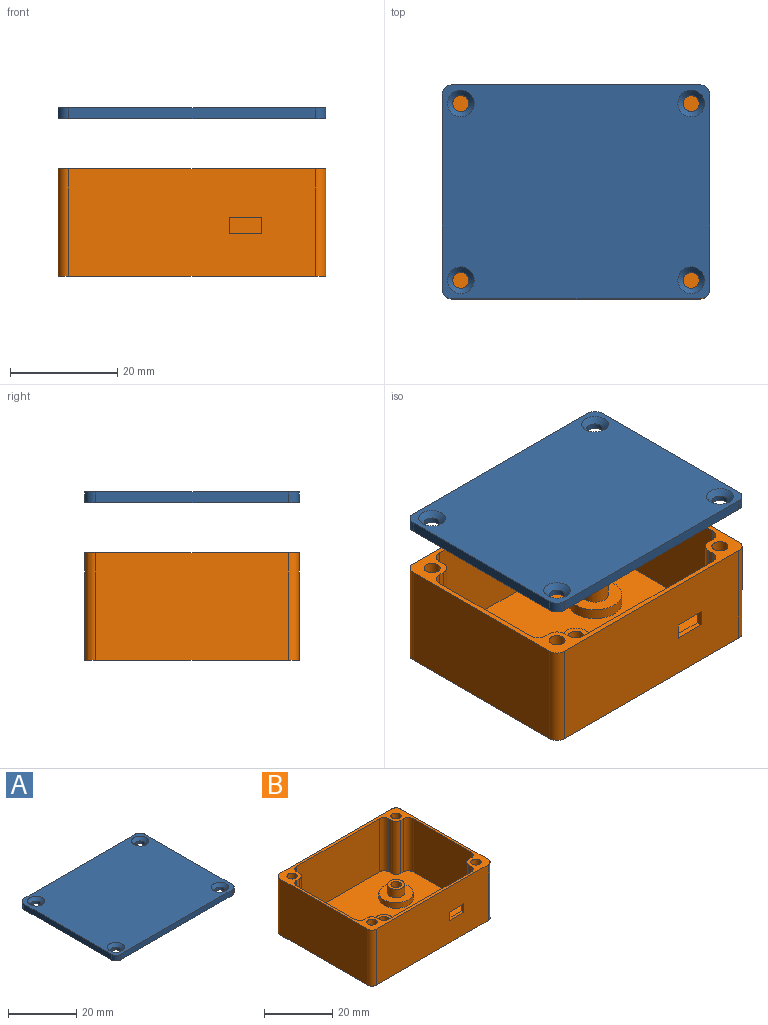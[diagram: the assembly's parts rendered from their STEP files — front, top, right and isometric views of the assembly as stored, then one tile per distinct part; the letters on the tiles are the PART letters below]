
ASSEMBLY  parts=2 mates=1
PART A: 18 faces, bbox 50x40x2 mm
  f0: plane 46x2mm, normal (0,1,0), area 92mm2, adj f4,f5,f14,f17
  f1: plane 36x2mm, normal (-1,0,0), area 72mm2, adj f4,f5,f14,f15
  f2: plane 46x2mm, normal (0,-1,0), area 92mm2, adj f4,f5,f15,f16
  f3: plane 36x2mm, normal (1,0,0), area 72mm2, adj f4,f5,f16,f17
  f4: plane 50x40mm, normal (0,0,1), area 1918mm2, adj f0,f1,f2,f3,f10,f11,f12,f13
  f5: plane 50x40mm, normal (0,0,-1), area 1968.3mm2, adj f0,f1,f2,f3,f6,f7,f8,f9
  f6: cylinder r=1.5mm len=3mm, axis (0,0,1), area 9.4mm2, adj f5,f10
  f7: cylinder r=1.5mm len=3mm, axis (0,0,1), area 9.4mm2, adj f5,f13
  f8: cylinder r=1.5mm len=3mm, axis (0,0,1), area 9.4mm2, adj f5,f12
  f9: cylinder r=1.5mm len=3mm, axis (0,0,1), area 9.4mm2, adj f5,f11
  f10: cone r=1.5mm half-angle=45deg, axis (0,0,1), area 17.8mm2, adj f4,f6
  f11: cone r=1.5mm half-angle=45deg, axis (0,0,1), area 17.8mm2, adj f4,f9
  f12: cone r=1.5mm half-angle=45deg, axis (0,0,1), area 17.8mm2, adj f4,f8
  f13: cone r=1.5mm half-angle=45deg, axis (0,0,1), area 17.8mm2, adj f4,f7
  f14: cylinder r=2mm len=2mm, axis (0,0,1), area 6.3mm2, adj f0,f1,f4,f5
  f15: cylinder r=2mm len=2mm, axis (0,0,-1), area 6.3mm2, adj f1,f2,f4,f5
  f16: cylinder r=2mm len=2mm, axis (0,0,1), area 6.3mm2, adj f2,f3,f4,f5
  f17: cylinder r=2mm len=2mm, axis (0,0,-1), area 6.3mm2, adj f0,f3,f4,f5
PART B: 71 faces, bbox 50x40x20 mm
  f0: plane 34x19mm, normal (0,1,0), area 628mm2, adj f5,f9,f56,f58,f67,f68,f69,f70
  f1: plane 46x20mm, normal (0,-1,0), area 902mm2, adj f2,f9,f52,f53,f67,f68,f69,f70
  f2: plane 50x40mm, normal (0,0,-1), area 1949.8mm2, adj f1,f10,f11,f12,f37,f38,f39,f40
  f3: cylinder r=1.5mm len=4mm, axis (0,0,-1), area 37.7mm2, adj f30,f50
  f4: cylinder r=1.5mm len=4mm, axis (0,0,-1), area 37.7mm2, adj f32,f43
  f5: plane 48x38mm, normal (0,0,1), area 1563.5mm2, adj f0,f6,f7,f8,f13,f14,f15,f16
  f6: plane 24x19mm, normal (1,0,0), area 456mm2, adj f5,f9,f57,f66
  f7: plane 34x19mm, normal (0,-1,0), area 646mm2, adj f5,f9,f62,f64
  f8: plane 24x19mm, normal (-1,0,0), area 456mm2, adj f5,f9,f60,f61
  f9: plane 50x40mm, normal (0,0,1), area 247.7mm2, adj f0,f1,f6,f7,f8,f10,f11,f12
  f10: plane 46x20mm, normal (0,1,0), area 920mm2, adj f2,f9,f51,f54
  f11: plane 36x20mm, normal (-1,0,0), area 720mm2, adj f2,f9,f51,f52
  f12: plane 36x20mm, normal (1,0,0), area 720mm2, adj f2,f9,f53,f54
  f13: plane 19x1mm, normal (0,-1,0), area 19mm2, adj f5,f9,f65,f66
  f14: plane 19x1mm, normal (1,0,0), area 19mm2, adj f5,f9,f64,f65
  f15: plane 19x1mm, normal (0,1,0), area 19mm2, adj f5,f9,f59,f60
  f16: plane 19x1mm, normal (-1,0,0), area 19mm2, adj f5,f9,f58,f59
  f17: plane 19x1mm, normal (0,-1,0), area 19mm2, adj f5,f9,f61,f63
  f18: plane 19x1mm, normal (-1,0,0), area 19mm2, adj f5,f9,f62,f63
  f19: plane 19x1mm, normal (0,1,0), area 19mm2, adj f5,f9,f55,f57
  f20: plane 19x1mm, normal (1,0,0), area 19mm2, adj f5,f9,f55,f56
  f21: cylinder r=1.5mm len=10mm, axis (0,0,1), area 94.2mm2, adj f9,f22
  f22: plane 3x3mm, normal (0,0,1), area 7.1mm2, adj f21
  f23: cylinder r=1.5mm len=10mm, axis (0,0,1), area 94.2mm2, adj f9,f24
  f24: plane 3x3mm, normal (0,0,1), area 7.1mm2, adj f23
  f25: cylinder r=1.5mm len=10mm, axis (0,0,1), area 94.2mm2, adj f9,f26
  f26: plane 3x3mm, normal (0,0,1), area 7.1mm2, adj f25
  f27: cylinder r=1.5mm len=10mm, axis (0,0,1), area 94.2mm2, adj f9,f28
  f28: plane 3x3mm, normal (0,0,1), area 7.1mm2, adj f27
  f29: cylinder r=2.5mm len=5mm, axis (0,0,-1), area 47.1mm2, adj f30,f34
  f30: plane 5x5mm, normal (0,0,1), area 12.6mm2, adj f3,f29
  f31: cylinder r=2.5mm len=5mm, axis (0,0,-1), area 47.1mm2, adj f32,f36
  f32: plane 5x5mm, normal (0,0,1), area 12.6mm2, adj f4,f31
  f33: cylinder r=5mm len=10mm, axis (0,0,-1), area 62.8mm2, adj f5,f34
  f34: plane 10x10mm, normal (0,0,1), area 58.9mm2, adj f29,f33
  f35: cylinder r=5mm len=10mm, axis (0,0,-1), area 62.8mm2, adj f5,f36
  f36: plane 10x10mm, normal (0,0,1), area 58.9mm2, adj f31,f35
  f37: plane 2.84x2mm, normal (-0.95,-0.32,0), area 6mm2, adj f2,f38,f42,f43
  f38: plane 2.26x2mm, normal (-0.75,0.66,0), area 6mm2, adj f2,f37,f39,f43
  f39: plane 2.94x2mm, normal (0.19,0.98,0), area 6mm2, adj f2,f38,f40,f43
  f40: plane 2.84x2mm, normal (0.95,0.32,0), area 6mm2, adj f2,f39,f41,f43
  f41: plane 2.26x2mm, normal (0.75,-0.66,0), area 6mm2, adj f2,f40,f42,f43
  f42: plane 2.94x2mm, normal (-0.19,-0.98,0), area 6mm2, adj f2,f37,f41,f43
  f43: plane 5.89x5.68mm, normal (0,0,-1), area 16.3mm2, adj f4,f37,f38,f39,f40,f41,f42
  f44: plane 3x2mm, normal (-1,-0.04,0), area 6mm2, adj f2,f45,f49,f50
  f45: plane 2.54x2mm, normal (-0.53,0.85,0), area 6mm2, adj f2,f44,f46,f50
  f46: plane 2.65x2mm, normal (0.47,0.88,0), area 6mm2, adj f2,f45,f47,f50
  f47: plane 3x2mm, normal (1,0.04,0), area 6mm2, adj f2,f46,f48,f50
  f48: plane 2.54x2mm, normal (0.53,-0.85,0), area 6mm2, adj f2,f47,f49,f50
  f49: plane 2.65x2mm, normal (-0.47,-0.88,0), area 6mm2, adj f2,f44,f48,f50
  f50: plane 6x5.31mm, normal (0,0,-1), area 16.3mm2, adj f3,f44,f45,f46,f47,f48,f49
  f51: cylinder r=2mm len=20mm, axis (0,0,1), area 62.8mm2, adj f2,f9,f10,f11
  f52: cylinder r=2mm len=20mm, axis (0,0,-1), area 62.8mm2, adj f1,f2,f9,f11
  f53: cylinder r=2mm len=20mm, axis (0,0,1), area 62.8mm2, adj f1,f2,f9,f12
  f54: cylinder r=2mm len=20mm, axis (0,0,-1), area 62.8mm2, adj f2,f9,f10,f12
  f55: cylinder r=2mm len=19mm, axis (0,0,1), area 59.7mm2, adj f5,f9,f19,f20
  f56: cylinder r=2mm len=19mm, axis (0,0,-1), area 59.7mm2, adj f0,f5,f9,f20
  f57: cylinder r=2mm len=19mm, axis (0,0,1), area 59.7mm2, adj f5,f6,f9,f19
  f58: cylinder r=2mm len=19mm, axis (0,0,1), area 59.7mm2, adj f0,f5,f9,f16
  f59: cylinder r=2mm len=19mm, axis (0,0,1), area 59.7mm2, adj f5,f9,f15,f16
  f60: cylinder r=2mm len=19mm, axis (0,0,1), area 59.7mm2, adj f5,f8,f9,f15
  f61: cylinder r=2mm len=19mm, axis (0,0,-1), area 59.7mm2, adj f5,f8,f9,f17
  f62: cylinder r=2mm len=19mm, axis (0,0,1), area 59.7mm2, adj f5,f7,f9,f18
  f63: cylinder r=2mm len=19mm, axis (0,0,1), area 59.7mm2, adj f5,f9,f17,f18
  f64: cylinder r=2mm len=19mm, axis (0,0,-1), area 59.7mm2, adj f5,f7,f9,f14
  f65: cylinder r=2mm len=19mm, axis (0,0,1), area 59.7mm2, adj f5,f9,f13,f14
  f66: cylinder r=2mm len=19mm, axis (0,0,-1), area 59.7mm2, adj f5,f6,f9,f13
  f67: plane 6x1mm, normal (0,0,-1), area 6mm2, adj f0,f1,f68,f70
  f68: plane 3x1mm, normal (1,0,0), area 3mm2, adj f0,f1,f67,f69
  f69: plane 6x1mm, normal (0,0,1), area 6mm2, adj f0,f1,f68,f70
  f70: plane 3x1mm, normal (-1,0,0), area 3mm2, adj f0,f1,f67,f69
PLACE A t=(-1.4,81.72,29.4)mm
PLACE B at identity fixed
MATE slider A.f8 <-> B.f25  axis (0,0,-1) through (-17.21,20.37,29.4)mm
